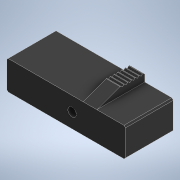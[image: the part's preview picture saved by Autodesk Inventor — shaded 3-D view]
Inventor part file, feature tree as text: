
AUTODESK INVENTOR PART (.ipt)
format: ipt  version: 2021 (Build 250183000, 183)  size: 165,376 bytes
history: native  units: mm
features: extrude x3, sketch x3, chamfer x1, projected_geometry x1
ambient origin geometry x8: Origin, YZ Plane, XZ Plane, XY Plane, X Axis, Y Axis, Z Axis, Center Point
bodies: Solid1 (feature_tree)
feature tree (8):
  extrude  "Extrusion1"  Depth=39.7mm
  extrude  "Extrusion2"  Depth=2.8mm
  extrude  "Extrusion3"  Depth=10.0mm
  chamfer  "Chamfer1"  Distance=1.0mm
  sketch  "Sketch1"  dims[d0=9.7mm d1=39.7mm]
  sketch  "Sketch2"  dims[d2=4.6mm d3=2.8mm]
  projected_geometry  "Projected Loop1"
  sketch  "Sketch3"  dims[d4=16.0mm d5=0.0mm d8=0.75mm d9=1.0mm d11=0.0mm d12=0.0mm d13=0.25mm d14=0.25mm d15=0.25mm d16=0.25mm d17=0.25mm d18=0.25mm d19=2.0mm d20=2.8mm d21=10.0mm d22=0.0mm d23=0.5mm d24=8.0mm d25=45.0deg d26=0.5mm d28=8.0mm]
